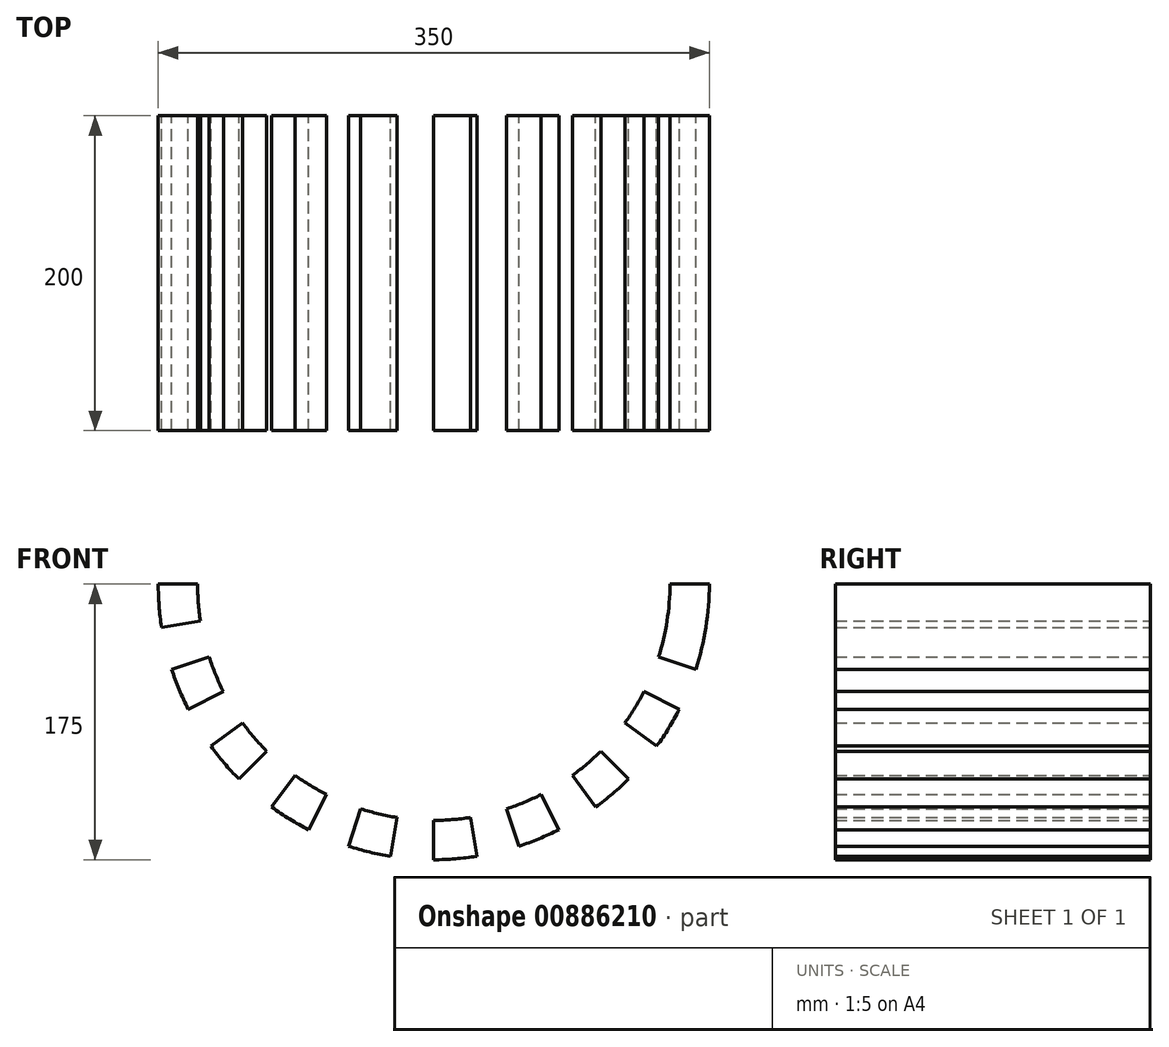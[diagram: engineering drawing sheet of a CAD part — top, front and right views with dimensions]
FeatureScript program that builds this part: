
annotation { "Feature Type Name" : "Feature", "Feature Type Description" : "" }
export const myFeature = defineFeature(function(context is Context, id is Id, definition is map)
    precondition{}
    {
        {
            var Q0;
            Q0=qCreatedBy(makeId("Front.planeOp"),FACE);
            var sketch = newSketch(context, id + "F0", { "sketchPlane" : qUnion([Q0])});
            skArc(sketch, "E0", {"start": v(-175, 0) * mm, "mid": v(-174.46, -13.73) * mm, "end": v(-172.85, -27.38) * mm});
            skArc(sketch, "E1", {"start": v(-150, 0) * mm, "mid": v(-149.54, -11.77) * mm, "end": v(-148.15, -23.47) * mm});
            skLineSegment(sketch, "E2", {"start": v(-150, 0) * mm, "end": v(-175, 0) * mm});
            skLineSegment(sketch, "E3", {"start": v(150, 0) * mm, "end": v(175, 0) * mm});
            skLineSegment(sketch, "E4", {"start": v(-148.15, -23.47) * mm, "end": v(-172.85, -27.38) * mm});
            skLineSegment(sketch, "E5", {"start": v(-142.66, -46.35) * mm, "end": v(-166.43, -54.08) * mm});
            skLineSegment(sketch, "E6", {"start": v(-133.65, -68.1) * mm, "end": v(-155.93, -79.45) * mm});
            skLineSegment(sketch, "E7", {"start": v(-121.35, -88.17) * mm, "end": v(-141.58, -102.86) * mm});
            skLineSegment(sketch, "E8", {"start": v(-106.07, -106.07) * mm, "end": v(-123.74, -123.74) * mm});
            skLineSegment(sketch, "E9", {"start": v(-88.17, -121.35) * mm, "end": v(-102.86, -141.58) * mm});
            skLineSegment(sketch, "E10", {"start": v(-68.1, -133.65) * mm, "end": v(-79.45, -155.93) * mm});
            skLineSegment(sketch, "E11", {"start": v(-46.35, -142.66) * mm, "end": v(-54.08, -166.43) * mm});
            skLineSegment(sketch, "E12", {"start": v(-23.47, -148.15) * mm, "end": v(-27.38, -172.85) * mm});
            skLineSegment(sketch, "E13", {"start": v(0, -150) * mm, "end": v(0, -175) * mm});
            skLineSegment(sketch, "E14", {"start": v(23.47, -148.15) * mm, "end": v(27.38, -172.85) * mm});
            skLineSegment(sketch, "E15", {"start": v(46.35, -142.66) * mm, "end": v(54.08, -166.43) * mm});
            skLineSegment(sketch, "E16", {"start": v(68.1, -133.65) * mm, "end": v(79.45, -155.93) * mm});
            skLineSegment(sketch, "E17", {"start": v(88.17, -121.35) * mm, "end": v(102.86, -141.58) * mm});
            skLineSegment(sketch, "E18", {"start": v(106.07, -106.07) * mm, "end": v(123.74, -123.74) * mm});
            skLineSegment(sketch, "E19", {"start": v(121.35, -88.17) * mm, "end": v(141.58, -102.86) * mm});
            skLineSegment(sketch, "E20", {"start": v(142.66, -46.35) * mm, "end": v(166.43, -54.08) * mm});
            skArc(sketch, "E21.trimOffspring", {"start": v(-142.66, -46.35) * mm, "mid": v(-138.58, -57.4) * mm, "end": v(-133.65, -68.1) * mm});
            skArc(sketch, "E22.trimOffspring", {"start": v(-166.43, -54.08) * mm, "mid": v(-161.68, -66.97) * mm, "end": v(-155.93, -79.45) * mm});
            skArc(sketch, "E23.trimOffspring", {"start": v(-121.35, -88.17) * mm, "mid": v(-114.06, -97.42) * mm, "end": v(-106.07, -106.07) * mm});
            skArc(sketch, "E24.trimOffspring", {"start": v(-141.58, -102.86) * mm, "mid": v(-133.07, -113.65) * mm, "end": v(-123.74, -123.74) * mm});
            skArc(sketch, "E25.trimOffspring", {"start": v(-88.17, -121.35) * mm, "mid": v(-78.37, -127.9) * mm, "end": v(-68.1, -133.65) * mm});
            skArc(sketch, "E26.trimOffspring", {"start": v(-102.86, -141.58) * mm, "mid": v(-91.44, -149.21) * mm, "end": v(-79.45, -155.93) * mm});
            skArc(sketch, "E27.trimOffspring", {"start": v(-46.35, -142.66) * mm, "mid": v(-35.02, -145.86) * mm, "end": v(-23.47, -148.15) * mm});
            skArc(sketch, "E28.trimOffspring", {"start": v(-54.08, -166.43) * mm, "mid": v(-40.85, -170.16) * mm, "end": v(-27.38, -172.85) * mm});
            skArc(sketch, "E29.trimOffspring", {"start": v(0, -150) * mm, "mid": v(11.77, -149.54) * mm, "end": v(23.47, -148.15) * mm});
            skArc(sketch, "E30.trimOffspring", {"start": v(0, -175) * mm, "mid": v(13.73, -174.46) * mm, "end": v(27.38, -172.85) * mm});
            skArc(sketch, "E31.trimOffspring", {"start": v(46.35, -142.66) * mm, "mid": v(57.4, -138.58) * mm, "end": v(68.1, -133.65) * mm});
            skArc(sketch, "E32.trimOffspring", {"start": v(54.08, -166.43) * mm, "mid": v(66.97, -161.68) * mm, "end": v(79.45, -155.93) * mm});
            skArc(sketch, "E33.trimOffspring", {"start": v(88.17, -121.35) * mm, "mid": v(97.42, -114.06) * mm, "end": v(106.07, -106.07) * mm});
            skArc(sketch, "E34.trimOffspring", {"start": v(102.86, -141.58) * mm, "mid": v(113.65, -133.07) * mm, "end": v(123.74, -123.74) * mm});
            skArc(sketch, "E35.trimOffspring", {"start": v(121.35, -88.17) * mm, "mid": v(127.9, -78.37) * mm, "end": v(133.65, -68.1) * mm});
            skArc(sketch, "E36.trimOffspring", {"start": v(141.58, -102.86) * mm, "mid": v(149.21, -91.44) * mm, "end": v(155.93, -79.45) * mm});
            skArc(sketch, "E37.trimOffspring", {"start": v(142.66, -46.35) * mm, "mid": v(148.15, -23.47) * mm, "end": v(150, 0) * mm});
            skArc(sketch, "E38.trimOffspring", {"start": v(166.43, -54.08) * mm, "mid": v(172.85, -27.38) * mm, "end": v(175, 0) * mm});
            skLineSegment(sketch, "E39", {"start": v(133.65, -68.1) * mm, "end": v(155.93, -79.45) * mm});
            skSolve(sketch);
        }
        {
            var Q0;
            Q0 = qSketchRegion(id + "F0", true);
            extrude(context, id + "F1", {"entities" : qUnion([Q0]), "depth" : 200 * mm, "offsetDistance" : 25 * mm});
        }
    });
